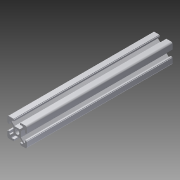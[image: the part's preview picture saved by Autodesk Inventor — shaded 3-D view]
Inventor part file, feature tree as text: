
AUTODESK INVENTOR PART (.ipt)
format: ipt  version: 2015 SP1 (Build 190203100, 203)  size: 153,600 bytes
history: native  units: mm
features: extrude x2, mirror x2, sketch x2, fillet x1
ambient origin geometry x8: Origin, YZ Plane, XZ Plane, XY Plane, X Axis, Y Axis, Z Axis, Center Point
bodies: Solid1 (feature_tree)
feature tree (7):
  extrude  "Extrusion1"  Depth=10.0mm
  fillet  "Fillet1"  Radius=10.0mm
  mirror  "Mirror1"
  mirror  "Mirror2"
  extrude  "Extrusion2"  Depth=6.1mm
  sketch  "Sketch1"  dims[d0=45.0deg d1=5.63mm d2=10.0mm]
  sketch  "Sketch2"  dims[d3=3.1mm d5=6.1mm d6=1.5mm d7=2.0mm d8=150.0mm d9=0.0mm d10=1.5mm d11=3.6mm d12=4.45mm d13=10.0mm d14=0.0mm]
